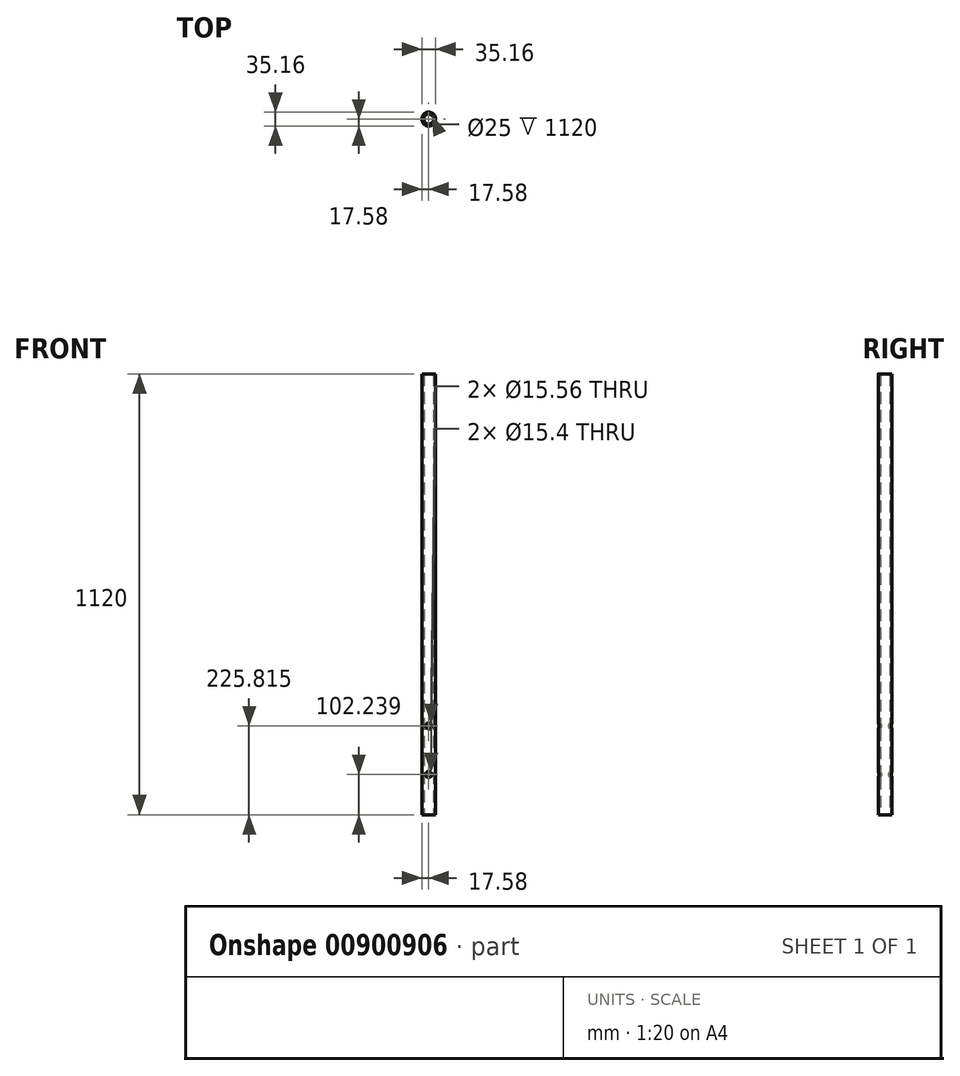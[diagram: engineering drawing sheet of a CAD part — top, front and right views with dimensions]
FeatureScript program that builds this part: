
annotation { "Feature Type Name" : "Feature", "Feature Type Description" : "" }
export const myFeature = defineFeature(function(context is Context, id is Id, definition is map)
    precondition{}
    {
        {
            var Q0;
            Q0=qCreatedBy(makeId("Top.planeOp"),FACE);
            var sketch = newSketch(context, id + "F0", { "sketchPlane" : qUnion([Q0])});
            skCircle(sketch, "E0", {"center": v(0, 0) * mm, "radius": 17.58 * mm});
            skSolve(sketch);
        }
        {
            var Q0;
            Q0 = qSketchRegion(id + "F0", true);
            extrude(context, id + "F1", {"entities" : qUnion([Q0]), "depth" : 1120 * mm, "offsetDistance" : 25 * mm});
        }
        {
            var Q0;
            Q0=sQuery(id+"F0.wireOp",VERTEX,"E0.center");
            var Q1;
            Q1=makeQuery(id+"F1.opExtrude","SWEPT_BODY",BODY,{"disambiguationData":[OSD([sQuery(id+"F0.wireOp",EDGE,"E0")])]});
            hole(context, id + "F2", {"style" : HoleStyle.SIMPLE, "endStyle" : HoleEndStyle.THROUGH, "oppositeDirection" : true, "holeDiameter" : 25 * mm, "majorDiameter" : 5 * mm, "isTappedThrough" : true, "tappedDepth" : 12 * mm, "tapClearance" : 3, "locations" : qUnion([Q0]), "scope" : qUnion([Q1])});
        }
        {
            var Q0;
            Q0=qCreatedBy(makeId("Front.planeOp"),FACE);
            var sketch = newSketch(context, id + "F3", { "sketchPlane" : qUnion([Q0])});
            skCircle(sketch, "E1", {"center": v(0, 102.24) * mm, "radius": 7.7 * mm});
            skCircle(sketch, "E2", {"center": v(0, 225.81) * mm, "radius": 7.78 * mm});
            skSolve(sketch);
        }
        {
            var Q0;
            Q0 = qSketchRegion(id + "F3", true);
            extrude(context, id + "F4", {"entities" : qUnion([Q0]), "operationType" : NewBodyOperationType.REMOVE, "oppositeDirection" : true, "depth" : 100 * mm, "offsetDistance" : 25 * mm});
        }
        {
            var Q0;
            Q0 = qSketchRegion(id + "F3", true);
            extrude(context, id + "F5", {"entities" : qUnion([Q0]), "operationType" : NewBodyOperationType.REMOVE, "depth" : 25 * mm, "offsetDistance" : 25 * mm});
        }
    });
